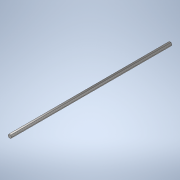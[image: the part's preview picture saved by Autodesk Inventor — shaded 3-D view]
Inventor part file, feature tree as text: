
AUTODESK INVENTOR PART (.ipt)
format: ipt  version: 2020 (Build 240168000, 168)  size: 108,032 bytes
history: native  units: in
note: dims shown in document units (in); Inventor stores cm internally (conversion verified against a paired STEP export)
features: extrude x1, sketch x1
ambient origin geometry x8: Origin, YZ Plane, XZ Plane, XY Plane, X Axis, Y Axis, Z Axis, Center Point
bodies: Solid1 (feature_tree)
feature tree (2):
  extrude  "Extrusion1"  Depth=26.0in TaperAngle=0.0deg
  sketch  "Sketch1"  dims[d0=0.5in d1=26.0in d2=0.0in]
